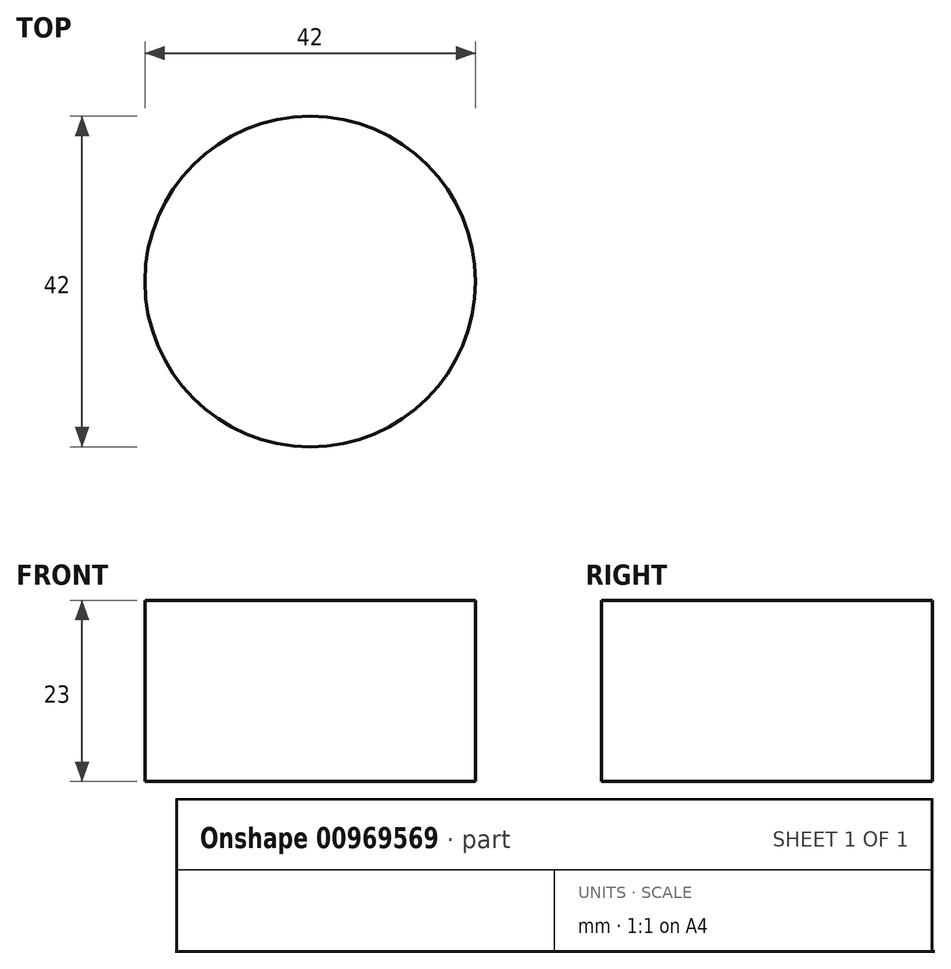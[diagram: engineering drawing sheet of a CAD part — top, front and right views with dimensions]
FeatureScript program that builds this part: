
annotation { "Feature Type Name" : "Feature", "Feature Type Description" : "" }
export const myFeature = defineFeature(function(context is Context, id is Id, definition is map)
    precondition{}
    {
        {
            var Q0;
            Q0=qCreatedBy(makeId("Top.planeOp"),FACE);
            var sketch = newSketch(context, id + "F0", { "sketchPlane" : qUnion([Q0])});
            skCircle(sketch, "E0", {"center": v(0, 0) * mm, "radius": 21 * mm});
            skSolve(sketch);
        }
        {
            var Q0;
            Q0 = qSketchRegion(id + "F0", true);
            extrude(context, id + "F1", {"entities" : qUnion([Q0]), "depth" : 23 * mm, "offsetDistance" : 25 * mm});
        }
    });
